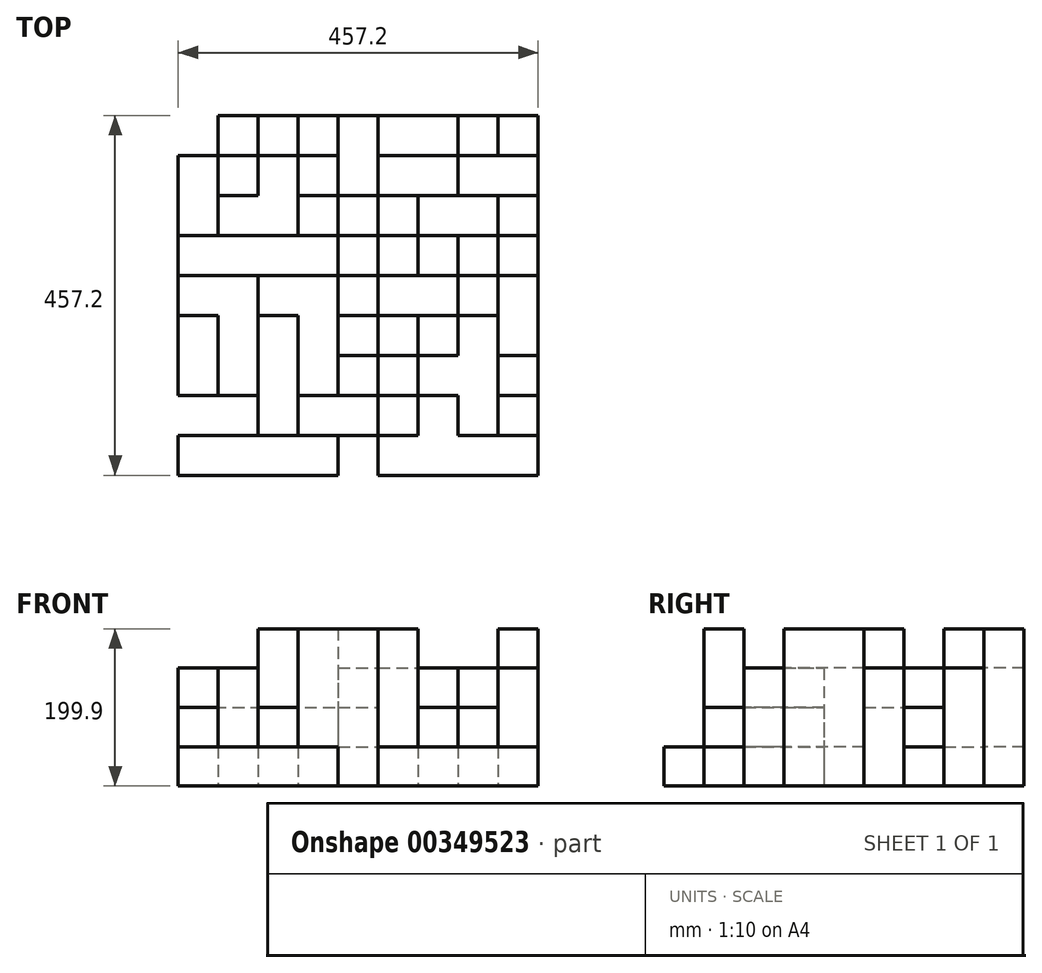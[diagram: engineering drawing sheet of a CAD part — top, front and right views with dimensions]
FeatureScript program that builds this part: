
annotation { "Feature Type Name" : "Feature", "Feature Type Description" : "" }
export const myFeature = defineFeature(function(context is Context, id is Id, definition is map)
    precondition{}
    {
        {
            var Q0;
            Q0=qCreatedBy(makeId("Top.planeOp"),FACE);
            var sketch = newSketch(context, id + "F0", { "sketchPlane" : qUnion([Q0])});
            skLineSegment(sketch, "E0.bottom", {"start": v(-228.6, 228.6) * mm, "end": v(228.6, 228.6) * mm});
            skLineSegment(sketch, "E0.top", {"start": v(-228.6, -228.6) * mm, "end": v(228.6, -228.6) * mm});
            skLineSegment(sketch, "E0.left", {"start": v(-228.6, 228.6) * mm, "end": v(-228.6, -228.6) * mm});
            skLineSegment(sketch, "E0.right", {"start": v(228.6, 228.6) * mm, "end": v(228.6, -228.6) * mm});
            skPoint(sketch, "E0.middle", {"position": v(0, 0) * mm});
            skLineSegment(sketch, "E1.bottom", {"start": v(-228.6, 228.6) * mm, "end": v(-177.8, 228.6) * mm});
            skLineSegment(sketch, "E1.top", {"start": v(-228.6, 177.8) * mm, "end": v(-177.8, 177.8) * mm});
            skLineSegment(sketch, "E1.left", {"start": v(-228.6, 228.6) * mm, "end": v(-228.6, 177.8) * mm});
            skLineSegment(sketch, "E1.right", {"start": v(-177.8, 228.6) * mm, "end": v(-177.8, 177.8) * mm});
            skLineSegment(sketch, "E2.MirrorCS", {"start": v(685.8, 177.8) * mm, "end": v(635, 177.8) * mm});
            skLineSegment(sketch, "E3.MirrorCS", {"start": v(635, 228.6) * mm, "end": v(635, 177.8) * mm});
            skLineSegment(sketch, "E4.bottom", {"start": v(-177.8, 228.6) * mm, "end": v(-127, 228.6) * mm});
            skLineSegment(sketch, "E4.top", {"start": v(-177.8, 177.8) * mm, "end": v(-127, 177.8) * mm});
            skLineSegment(sketch, "E4.right", {"start": v(-127, 228.6) * mm, "end": v(-127, 177.8) * mm});
            skLineSegment(sketch, "E5.bottom", {"start": v(-127, 177.8) * mm, "end": v(-76.2, 177.8) * mm});
            skLineSegment(sketch, "E5.top", {"start": v(-127, 228.6) * mm, "end": v(-76.2, 228.6) * mm});
            skLineSegment(sketch, "E5.left", {"start": v(-127, 177.8) * mm, "end": v(-127, 228.6) * mm});
            skLineSegment(sketch, "E6.bottom", {"start": v(-76.2, 228.6) * mm, "end": v(-25.4, 228.6) * mm});
            skLineSegment(sketch, "E6.right", {"start": v(-25.4, 228.6) * mm, "end": v(-25.4, 177.8) * mm});
            skLineSegment(sketch, "E7.bottom", {"start": v(-25.4, 228.6) * mm, "end": v(25.4, 228.6) * mm});
            skLineSegment(sketch, "E7.top", {"start": v(-25.4, 177.8) * mm, "end": v(25.4, 177.8) * mm});
            skLineSegment(sketch, "E7.right", {"start": v(25.4, 228.6) * mm, "end": v(25.4, 177.8) * mm});
            skLineSegment(sketch, "E8.bottom", {"start": v(25.42, 228.6) * mm, "end": v(76.22, 228.6) * mm});
            skLineSegment(sketch, "E8.top", {"start": v(25.42, 177.8) * mm, "end": v(76.22, 177.8) * mm});
            skLineSegment(sketch, "E8.left", {"start": v(25.42, 228.6) * mm, "end": v(25.42, 177.8) * mm});
            skLineSegment(sketch, "E8.right", {"start": v(76.22, 228.6) * mm, "end": v(76.22, 177.8) * mm});
            skLineSegment(sketch, "E9.bottom", {"start": v(76.22, 228.6) * mm, "end": v(127.02, 228.6) * mm});
            skLineSegment(sketch, "E9.top", {"start": v(76.22, 177.8) * mm, "end": v(127.02, 177.8) * mm});
            skLineSegment(sketch, "E9.right", {"start": v(127.02, 228.6) * mm, "end": v(127.02, 177.8) * mm});
            skLineSegment(sketch, "E10.bottom", {"start": v(127.02, 228.6) * mm, "end": v(177.82, 228.6) * mm});
            skLineSegment(sketch, "E10.top", {"start": v(127.02, 177.8) * mm, "end": v(177.82, 177.8) * mm});
            skLineSegment(sketch, "E10.right", {"start": v(177.82, 228.6) * mm, "end": v(177.82, 177.8) * mm});
            skLineSegment(sketch, "E11.bottom", {"start": v(177.82, 228.6) * mm, "end": v(228.62, 228.6) * mm});
            skLineSegment(sketch, "E11.top", {"start": v(177.82, 177.8) * mm, "end": v(228.62, 177.8) * mm});
            skLineSegment(sketch, "E11.right", {"start": v(228.62, 228.6) * mm, "end": v(228.62, 177.8) * mm});
            skLineSegment(sketch, "E12", {"start": v(-76.2, 228.6) * mm, "end": v(-76.2, 177.8) * mm});
            skLineSegment(sketch, "E13.bottom", {"start": v(-76.2, 177.8) * mm, "end": v(-25.4, 177.8) * mm});
            skLineSegment(sketch, "E13.top", {"start": v(-76.2, 177.8) * mm, "end": v(-25.4, 177.8) * mm});
            skLineSegment(sketch, "E13.left", {"start": v(-76.2, 177.8) * mm, "end": v(-76.2, 177.8) * mm});
            skLineSegment(sketch, "E13.right", {"start": v(-25.4, 177.8) * mm, "end": v(-25.4, 177.8) * mm});
            skLineSegment(sketch, "E14.MirrorCS", {"start": v(-228.6, 127) * mm, "end": v(-228.6, 177.8) * mm});
            skLineSegment(sketch, "E15.MirrorCS", {"start": v(-127, 127) * mm, "end": v(-127, 177.8) * mm});
            skLineSegment(sketch, "E16.MirrorCS", {"start": v(-76.2, 127) * mm, "end": v(-76.2, 177.8) * mm});
            skLineSegment(sketch, "E17.MirrorCS", {"start": v(-25.4, 127) * mm, "end": v(-25.4, 177.8) * mm});
            skLineSegment(sketch, "E18.MirrorCS", {"start": v(25.42, 127) * mm, "end": v(25.42, 177.8) * mm});
            skLineSegment(sketch, "E19.MirrorCS", {"start": v(-228.6, 127) * mm, "end": v(-177.8, 127) * mm});
            skLineSegment(sketch, "E20.MirrorCS", {"start": v(-127, 177.8) * mm, "end": v(-127, 127) * mm});
            skLineSegment(sketch, "E21.MirrorCS", {"start": v(127.02, 127) * mm, "end": v(127.02, 177.8) * mm});
            skLineSegment(sketch, "E22.MirrorCS", {"start": v(25.4, 127) * mm, "end": v(25.4, 177.8) * mm});
            skLineSegment(sketch, "E23.MirrorCS", {"start": v(-177.8, 127) * mm, "end": v(-177.8, 177.8) * mm});
            skLineSegment(sketch, "E24.MirrorCS", {"start": v(-177.8, 127) * mm, "end": v(-127, 127) * mm});
            skLineSegment(sketch, "E25.MirrorCS", {"start": v(76.22, 127) * mm, "end": v(76.22, 177.8) * mm});
            skLineSegment(sketch, "E26.MirrorCS", {"start": v(-25.4, 127) * mm, "end": v(25.4, 127) * mm});
            skLineSegment(sketch, "E27.MirrorCS", {"start": v(25.42, 127) * mm, "end": v(76.22, 127) * mm});
            skLineSegment(sketch, "E28.MirrorCS", {"start": v(76.22, 127) * mm, "end": v(127.02, 127) * mm});
            skLineSegment(sketch, "E29.MirrorCS", {"start": v(127.02, 127) * mm, "end": v(177.82, 127) * mm});
            skLineSegment(sketch, "E30.MirrorCS", {"start": v(-127, 127) * mm, "end": v(-76.2, 127) * mm});
            skLineSegment(sketch, "E31.MirrorCS", {"start": v(-228.6, 127) * mm, "end": v(228.6, 127) * mm});
            skLineSegment(sketch, "E32.MirrorCS", {"start": v(-76.2, 127) * mm, "end": v(-25.4, 127) * mm});
            skLineSegment(sketch, "E33.MirrorCS", {"start": v(177.82, 127) * mm, "end": v(177.82, 177.8) * mm});
            skLineSegment(sketch, "E34.MirrorCS", {"start": v(-76.2, 127) * mm, "end": v(-76.2, 76.2) * mm});
            skLineSegment(sketch, "E35.MirrorCS", {"start": v(-76.2, 25.4) * mm, "end": v(-76.2, 76.2) * mm});
            skLineSegment(sketch, "E36.MirrorCS", {"start": v(-177.8, 76.2) * mm, "end": v(-127, 76.2) * mm});
            skLineSegment(sketch, "E37.MirrorCS", {"start": v(-76.2, 76.2) * mm, "end": v(-25.4, 76.2) * mm});
            skLineSegment(sketch, "E38.MirrorCS", {"start": v(-25.4, 127) * mm, "end": v(-25.4, 76.2) * mm});
            skLineSegment(sketch, "E39.MirrorCS", {"start": v(-127, 25.4) * mm, "end": v(-127, 76.2) * mm});
            skLineSegment(sketch, "E40.MirrorCS", {"start": v(25.4, 25.4) * mm, "end": v(25.4, 76.2) * mm});
            skLineSegment(sketch, "E41.MirrorCS", {"start": v(-127, 127) * mm, "end": v(-127, 76.2) * mm});
            skLineSegment(sketch, "E42.MirrorCS", {"start": v(-25.4, 25.4) * mm, "end": v(-25.4, 76.2) * mm});
            skLineSegment(sketch, "E43.MirrorCS", {"start": v(25.4, 127) * mm, "end": v(25.4, 76.2) * mm});
            skLineSegment(sketch, "E44.MirrorCS", {"start": v(76.22, 127) * mm, "end": v(76.22, 76.2) * mm});
            skLineSegment(sketch, "E45.MirrorCS", {"start": v(-127, 76.2) * mm, "end": v(-127, 127) * mm});
            skLineSegment(sketch, "E46.MirrorCS", {"start": v(127.02, 127) * mm, "end": v(127.02, 76.2) * mm});
            skLineSegment(sketch, "E47.MirrorCS", {"start": v(76.22, 25.4) * mm, "end": v(76.22, 76.2) * mm});
            skLineSegment(sketch, "E48.MirrorCS", {"start": v(-25.4, 76.2) * mm, "end": v(25.4, 76.2) * mm});
            skLineSegment(sketch, "E49.MirrorCS", {"start": v(-25.4, 76.2) * mm, "end": v(-25.4, 76.2) * mm});
            skLineSegment(sketch, "E50.MirrorCS", {"start": v(-177.8, 25.4) * mm, "end": v(-177.8, 76.2) * mm});
            skLineSegment(sketch, "E51.MirrorCS", {"start": v(127.02, 76.2) * mm, "end": v(177.82, 76.2) * mm});
            skLineSegment(sketch, "E52.MirrorCS", {"start": v(25.42, 127) * mm, "end": v(25.42, 76.2) * mm});
            skLineSegment(sketch, "E53.MirrorCS", {"start": v(76.22, 76.2) * mm, "end": v(127.02, 76.2) * mm});
            skLineSegment(sketch, "E54.MirrorCS", {"start": v(-127, 76.2) * mm, "end": v(-127, 25.4) * mm});
            skLineSegment(sketch, "E55.MirrorCS", {"start": v(-76.2, 76.2) * mm, "end": v(-76.2, 76.2) * mm});
            skLineSegment(sketch, "E56.MirrorCS", {"start": v(25.42, 76.2) * mm, "end": v(76.22, 76.2) * mm});
            skLineSegment(sketch, "E57.MirrorCS", {"start": v(25.42, 25.4) * mm, "end": v(25.42, 76.2) * mm});
            skLineSegment(sketch, "E58.MirrorCS", {"start": v(127.02, 25.4) * mm, "end": v(127.02, 76.2) * mm});
            skLineSegment(sketch, "E59.MirrorCS", {"start": v(-177.8, 127) * mm, "end": v(-177.8, 76.2) * mm});
            skLineSegment(sketch, "E60.MirrorCS", {"start": v(-127, 76.2) * mm, "end": v(-76.2, 76.2) * mm});
            skLineSegment(sketch, "E61.MirrorCS", {"start": v(177.82, 25.4) * mm, "end": v(177.82, 76.2) * mm});
            skLineSegment(sketch, "E62.MirrorCS", {"start": v(-177.8, 25.4) * mm, "end": v(-127, 25.4) * mm});
            skLineSegment(sketch, "E63.MirrorCS", {"start": v(-25.4, 25.4) * mm, "end": v(25.4, 25.4) * mm});
            skLineSegment(sketch, "E64.MirrorCS", {"start": v(-76.2, 25.4) * mm, "end": v(-25.4, 25.4) * mm});
            skLineSegment(sketch, "E65.MirrorCS", {"start": v(76.22, 25.4) * mm, "end": v(127.02, 25.4) * mm});
            skLineSegment(sketch, "E66.MirrorCS", {"start": v(25.42, 25.4) * mm, "end": v(76.22, 25.4) * mm});
            skLineSegment(sketch, "E67.MirrorCS", {"start": v(127.02, 25.4) * mm, "end": v(177.82, 25.4) * mm});
            skLineSegment(sketch, "E68.MirrorCS", {"start": v(-127, 25.4) * mm, "end": v(-76.2, 25.4) * mm});
            skLineSegment(sketch, "E69.MirrorCS", {"start": v(177.82, 127) * mm, "end": v(177.82, 76.2) * mm});
            skLineSegment(sketch, "E70.MirrorCS", {"start": v(177.82, 76.2) * mm, "end": v(228.62, 76.2) * mm});
            skLineSegment(sketch, "E71.MirrorCS", {"start": v(-228.6, 76.2) * mm, "end": v(-177.8, 76.2) * mm});
            skLineSegment(sketch, "E72.MirrorCS", {"start": v(-228.6, 25.4) * mm, "end": v(-177.8, 25.4) * mm});
            skLineSegment(sketch, "E73.MirrorCS", {"start": v(-228.6, 25.4) * mm, "end": v(228.6, 25.4) * mm});
            skLineSegment(sketch, "E74.MirrorCS", {"start": v(-76.2, -76.2) * mm, "end": v(-76.2, -25.4) * mm});
            skLineSegment(sketch, "E75.MirrorCS", {"start": v(-76.2, -76.2) * mm, "end": v(-76.2, -127) * mm});
            skLineSegment(sketch, "E76.MirrorCS", {"start": v(-76.2, -177.8) * mm, "end": v(-76.2, -127) * mm});
            skLineSegment(sketch, "E77.MirrorCS", {"start": v(-76.2, -25.4) * mm, "end": v(-25.4, -25.4) * mm});
            skLineSegment(sketch, "E78.MirrorCS", {"start": v(-177.8, -25.4) * mm, "end": v(-127, -25.4) * mm});
            skLineSegment(sketch, "E79.MirrorCS", {"start": v(-76.2, -177.8) * mm, "end": v(-25.4, -177.8) * mm});
            skLineSegment(sketch, "E80.MirrorCS", {"start": v(-127, -177.8) * mm, "end": v(-76.2, -177.8) * mm});
            skLineSegment(sketch, "E81.MirrorCS", {"start": v(-76.2, -127) * mm, "end": v(-25.4, -127) * mm});
            skLineSegment(sketch, "E82.MirrorCS", {"start": v(127.02, -177.8) * mm, "end": v(177.82, -177.8) * mm});
            skLineSegment(sketch, "E83.MirrorCS", {"start": v(177.82, -177.8) * mm, "end": v(228.62, -177.8) * mm});
            skLineSegment(sketch, "E84.MirrorCS", {"start": v(-25.4, -177.8) * mm, "end": v(25.4, -177.8) * mm});
            skLineSegment(sketch, "E85.MirrorCS", {"start": v(-177.8, -127) * mm, "end": v(-127, -127) * mm});
            skLineSegment(sketch, "E86.MirrorCS", {"start": v(76.22, -76.2) * mm, "end": v(127.02, -76.2) * mm});
            skLineSegment(sketch, "E87.MirrorCS", {"start": v(25.42, -76.2) * mm, "end": v(76.22, -76.2) * mm});
            skLineSegment(sketch, "E88.MirrorCS", {"start": v(-127, -177.8) * mm, "end": v(-127, -127) * mm});
            skLineSegment(sketch, "E89.MirrorCS", {"start": v(-25.4, -76.2) * mm, "end": v(-25.4, -25.4) * mm});
            skLineSegment(sketch, "E90.MirrorCS", {"start": v(25.42, -177.8) * mm, "end": v(25.42, -127) * mm});
            skLineSegment(sketch, "E91.MirrorCS", {"start": v(25.42, -76.2) * mm, "end": v(25.42, -127) * mm});
            skLineSegment(sketch, "E92.MirrorCS", {"start": v(-127, -25.4) * mm, "end": v(-127, -76.2) * mm});
            skLineSegment(sketch, "E93.MirrorCS", {"start": v(-127, -76.2) * mm, "end": v(-127, -127) * mm});
            skLineSegment(sketch, "E94.MirrorCS", {"start": v(-25.4, -76.2) * mm, "end": v(-25.4, -127) * mm});
            skLineSegment(sketch, "E95.MirrorCS", {"start": v(-25.4, -177.8) * mm, "end": v(-25.4, -127) * mm});
            skLineSegment(sketch, "E96.MirrorCS", {"start": v(-228.6, -177.8) * mm, "end": v(228.6, -177.8) * mm});
            skLineSegment(sketch, "E97.MirrorCS", {"start": v(25.42, -76.2) * mm, "end": v(25.42, -25.4) * mm});
            skLineSegment(sketch, "E98.MirrorCS", {"start": v(127.02, -76.2) * mm, "end": v(177.82, -76.2) * mm});
            skLineSegment(sketch, "E99.MirrorCS", {"start": v(-177.8, -76.2) * mm, "end": v(-127, -76.2) * mm});
            skLineSegment(sketch, "E100.MirrorCS", {"start": v(25.42, -177.8) * mm, "end": v(76.22, -177.8) * mm});
            skLineSegment(sketch, "E101.MirrorCS", {"start": v(-127, -76.2) * mm, "end": v(-76.2, -76.2) * mm});
            skLineSegment(sketch, "E102.MirrorCS", {"start": v(-127, -76.2) * mm, "end": v(-127, -25.4) * mm});
            skLineSegment(sketch, "E103.MirrorCS", {"start": v(-177.8, -76.2) * mm, "end": v(-177.8, -25.4) * mm});
            skLineSegment(sketch, "E104.MirrorCS", {"start": v(-228.6, -76.2) * mm, "end": v(-177.8, -76.2) * mm});
            skLineSegment(sketch, "E105.MirrorCS", {"start": v(-127, -127) * mm, "end": v(-127, -177.8) * mm});
            skLineSegment(sketch, "E106.MirrorCS", {"start": v(76.22, -76.2) * mm, "end": v(76.22, -25.4) * mm});
            skLineSegment(sketch, "E107.MirrorCS", {"start": v(127.02, -127) * mm, "end": v(177.82, -127) * mm});
            skLineSegment(sketch, "E108.MirrorCS", {"start": v(25.4, -76.2) * mm, "end": v(25.4, -127) * mm});
            skLineSegment(sketch, "E109.MirrorCS", {"start": v(-25.4, -127) * mm, "end": v(25.4, -127) * mm});
            skLineSegment(sketch, "E110.MirrorCS", {"start": v(-76.2, -127) * mm, "end": v(-76.2, -127) * mm});
            skLineSegment(sketch, "E111.MirrorCS", {"start": v(76.22, -127) * mm, "end": v(127.02, -127) * mm});
            skLineSegment(sketch, "E112.MirrorCS", {"start": v(-177.8, -76.2) * mm, "end": v(-177.8, -127) * mm});
            skLineSegment(sketch, "E113.MirrorCS", {"start": v(-76.2, -25.4) * mm, "end": v(-76.2, -25.4) * mm});
            skLineSegment(sketch, "E114.MirrorCS", {"start": v(-25.4, -127) * mm, "end": v(-25.4, -127) * mm});
            skLineSegment(sketch, "E115.MirrorCS", {"start": v(127.02, -76.2) * mm, "end": v(127.02, -25.4) * mm});
            skLineSegment(sketch, "E116.MirrorCS", {"start": v(-127, -127) * mm, "end": v(-76.2, -127) * mm});
            skLineSegment(sketch, "E117.MirrorCS", {"start": v(127.02, -177.8) * mm, "end": v(127.02, -127) * mm});
            skLineSegment(sketch, "E118.MirrorCS", {"start": v(76.22, -25.4) * mm, "end": v(127.02, -25.4) * mm});
            skLineSegment(sketch, "E119.MirrorCS", {"start": v(127.02, -25.4) * mm, "end": v(177.82, -25.4) * mm});
            skLineSegment(sketch, "E120.MirrorCS", {"start": v(-127, -25.4) * mm, "end": v(-76.2, -25.4) * mm});
            skLineSegment(sketch, "E121.MirrorCS", {"start": v(-127, -127) * mm, "end": v(-127, -76.2) * mm});
            skLineSegment(sketch, "E122.MirrorCS", {"start": v(177.82, -177.8) * mm, "end": v(177.82, -127) * mm});
            skLineSegment(sketch, "E123.MirrorCS", {"start": v(25.4, -177.8) * mm, "end": v(25.4, -127) * mm});
            skLineSegment(sketch, "E124.MirrorCS", {"start": v(-76.2, -76.2) * mm, "end": v(-25.4, -76.2) * mm});
            skLineSegment(sketch, "E125.MirrorCS", {"start": v(-25.4, -25.4) * mm, "end": v(25.4, -25.4) * mm});
            skLineSegment(sketch, "E126.MirrorCS", {"start": v(127.02, -76.2) * mm, "end": v(127.02, -127) * mm});
            skLineSegment(sketch, "E127.MirrorCS", {"start": v(-25.4, -76.2) * mm, "end": v(25.4, -76.2) * mm});
            skLineSegment(sketch, "E128.MirrorCS", {"start": v(25.42, -127) * mm, "end": v(76.22, -127) * mm});
            skLineSegment(sketch, "E129.MirrorCS", {"start": v(76.22, -76.2) * mm, "end": v(76.22, -127) * mm});
            skLineSegment(sketch, "E130.MirrorCS", {"start": v(25.42, -25.4) * mm, "end": v(76.22, -25.4) * mm});
            skLineSegment(sketch, "E131.MirrorCS", {"start": v(-25.4, -25.4) * mm, "end": v(-25.4, -25.4) * mm});
            skLineSegment(sketch, "E132.MirrorCS", {"start": v(76.22, -177.8) * mm, "end": v(76.22, -127) * mm});
            skLineSegment(sketch, "E133.MirrorCS", {"start": v(-177.8, -177.8) * mm, "end": v(-127, -177.8) * mm});
            skLineSegment(sketch, "E134.MirrorCS", {"start": v(-177.8, -177.8) * mm, "end": v(-177.8, -127) * mm});
            skLineSegment(sketch, "E135.MirrorCS", {"start": v(177.82, -76.2) * mm, "end": v(177.82, -127) * mm});
            skLineSegment(sketch, "E136.MirrorCS", {"start": v(177.82, -76.2) * mm, "end": v(177.82, -25.4) * mm});
            skLineSegment(sketch, "E137.MirrorCS", {"start": v(228.62, -177.8) * mm, "end": v(228.62, -127) * mm});
            skLineSegment(sketch, "E138.MirrorCS", {"start": v(177.82, -127) * mm, "end": v(228.62, -127) * mm});
            skLineSegment(sketch, "E139.MirrorCS", {"start": v(177.82, -25.4) * mm, "end": v(228.62, -25.4) * mm});
            skLineSegment(sketch, "E140.MirrorCS", {"start": v(-228.6, -76.2) * mm, "end": v(-228.6, -127) * mm});
            skLineSegment(sketch, "E141.MirrorCS", {"start": v(-228.6, -25.4) * mm, "end": v(-177.8, -25.4) * mm});
            skLineSegment(sketch, "E142.MirrorCS", {"start": v(-228.6, -177.8) * mm, "end": v(-177.8, -177.8) * mm});
            skLineSegment(sketch, "E143.MirrorCS", {"start": v(-228.6, -127) * mm, "end": v(-177.8, -127) * mm});
            skLineSegment(sketch, "E144.MirrorCS", {"start": v(-228.6, -177.8) * mm, "end": v(-228.6, -127) * mm});
            skLineSegment(sketch, "E145.MirrorCS", {"start": v(-228.6, -76.2) * mm, "end": v(228.6, -76.2) * mm});
            skLineSegment(sketch, "E146.MirrorCS", {"start": v(25.4, -76.2) * mm, "end": v(25.4, -25.4) * mm});
            skLineSegment(sketch, "E147.MirrorCS", {"start": v(76.22, -177.8) * mm, "end": v(127.02, -177.8) * mm});
            skLineSegment(sketch, "E148.MirrorCS", {"start": v(-76.2, 25.4) * mm, "end": v(-76.2, -25.4) * mm});
            skLineSegment(sketch, "E149.MirrorCS", {"start": v(-25.4, 25.4) * mm, "end": v(-25.4, -25.4) * mm});
            skLineSegment(sketch, "E150.MirrorCS", {"start": v(25.4, 25.4) * mm, "end": v(25.4, -25.4) * mm});
            skLineSegment(sketch, "E151.MirrorCS", {"start": v(-127, 25.4) * mm, "end": v(-127, -25.4) * mm});
            skLineSegment(sketch, "E152.MirrorCS", {"start": v(-177.8, 25.4) * mm, "end": v(-177.8, -25.4) * mm});
            skLineSegment(sketch, "E153.MirrorCS", {"start": v(177.82, 25.4) * mm, "end": v(177.82, -25.4) * mm});
            skLineSegment(sketch, "E154.MirrorCS", {"start": v(-127, -25.4) * mm, "end": v(-127, 25.4) * mm});
            skLineSegment(sketch, "E155.MirrorCS", {"start": v(76.22, 25.4) * mm, "end": v(76.22, -25.4) * mm});
            skLineSegment(sketch, "E156.MirrorCS", {"start": v(127.02, 25.4) * mm, "end": v(127.02, -25.4) * mm});
            skLineSegment(sketch, "E157.MirrorCS", {"start": v(25.42, 25.4) * mm, "end": v(25.42, -25.4) * mm});
            skLineSegment(sketch, "E158.MirrorCS", {"start": v(-76.2, -228.6) * mm, "end": v(-25.4, -228.6) * mm});
            skLineSegment(sketch, "E159.MirrorCS", {"start": v(-177.8, -228.6) * mm, "end": v(-127, -228.6) * mm});
            skLineSegment(sketch, "E160.MirrorCS", {"start": v(-25.4, -228.6) * mm, "end": v(-25.4, -228.6) * mm});
            skLineSegment(sketch, "E161.MirrorCS", {"start": v(127.02, -228.6) * mm, "end": v(177.82, -228.6) * mm});
            skLineSegment(sketch, "E162.MirrorCS", {"start": v(-25.4, -228.6) * mm, "end": v(25.4, -228.6) * mm});
            skLineSegment(sketch, "E163.MirrorCS", {"start": v(-127, -228.6) * mm, "end": v(-76.2, -228.6) * mm});
            skLineSegment(sketch, "E164.MirrorCS", {"start": v(76.22, -228.6) * mm, "end": v(127.02, -228.6) * mm});
            skLineSegment(sketch, "E165.MirrorCS", {"start": v(-76.2, -228.6) * mm, "end": v(-76.2, -228.6) * mm});
            skLineSegment(sketch, "E166.MirrorCS", {"start": v(25.42, -228.6) * mm, "end": v(76.22, -228.6) * mm});
            skLineSegment(sketch, "E167.MirrorCS", {"start": v(177.82, -228.6) * mm, "end": v(228.62, -228.6) * mm});
            skLineSegment(sketch, "E168.MirrorCS", {"start": v(-228.6, -228.6) * mm, "end": v(-177.8, -228.6) * mm});
            skLineSegment(sketch, "E169.MirrorCS", {"start": v(177.82, -177.8) * mm, "end": v(177.82, -228.6) * mm});
            skLineSegment(sketch, "E170.MirrorCS", {"start": v(127.02, -177.8) * mm, "end": v(127.02, -228.6) * mm});
            skLineSegment(sketch, "E171.MirrorCS", {"start": v(76.22, -177.8) * mm, "end": v(76.22, -228.6) * mm});
            skLineSegment(sketch, "E172.MirrorCS", {"start": v(25.42, -177.8) * mm, "end": v(25.42, -228.6) * mm});
            skLineSegment(sketch, "E173.MirrorCS", {"start": v(-25.4, -177.8) * mm, "end": v(-25.4, -228.6) * mm});
            skLineSegment(sketch, "E174.MirrorCS", {"start": v(-76.2, -177.8) * mm, "end": v(-76.2, -228.6) * mm});
            skLineSegment(sketch, "E175.MirrorCS", {"start": v(-127, -177.8) * mm, "end": v(-127, -228.6) * mm});
            skLineSegment(sketch, "E176.MirrorCS", {"start": v(-177.8, -177.8) * mm, "end": v(-177.8, -228.6) * mm});
            skSolve(sketch);
        }
        {
            var Q0;
            {var subQ0=sQuery(id+"F0.wireOp",EDGE,"E50.MirrorCS");Q0=makeQuery(id+"F0.imprint","IMPRINT",FACE,{"disambiguationData":[TD([[makeQuery(id+"F0.imprint","IMPRINT",EDGE,{"derivedFrom":subQ0}),-1.0]])]});}
            var Q1;
            Q1=sQuery(id+"F0.wireOp",EDGE,"E0.top");
            revolve(context, id + "F1", {"entities" : qUnion([Q0]), "axis" : qUnion([Q1]), "revolveType" : RevolveType.FULL});
        }
        {
            var Q0;
            Q0=makeQuery(id+"F1.opRevolve","SWEPT_BODY",BODY,{"disambiguationData":[OSD([sQuery(id+"F0.wireOp",EDGE,"E50.MirrorCS"),sQuery(id+"F0.wireOp",EDGE,"E36.MirrorCS"),sQuery(id+"F0.wireOp",EDGE,"E39.MirrorCS"),sQuery(id+"F0.wireOp",EDGE,"E73.MirrorCS")])]});
            deleteBodies(context, id + "F2", {"entities" : qUnion([Q0])});
        }
        {
            var Q0;
            Q0=makeQuery(id+"F0.imprint","IMPRINT",FACE,{"disambiguationData":[TD([[makeQuery(id+"F0.imprint","IMPRINT",EDGE,{"derivedFrom":sQuery(id+"F0.wireOp",EDGE,"E13.bottom")}),1.0]])]});
            var Q1;
            {var subQ0=sQuery(id+"F0.wireOp",EDGE,"E9.right");Q1=makeQuery(id+"F0.imprint","IMPRINT",FACE,{"disambiguationData":[TD([[makeQuery(id+"F0.imprint","IMPRINT",EDGE,{"derivedFrom":subQ0}),1.0]])]});}
            var Q2;
            Q2=makeQuery(id+"F0.imprint","IMPRINT",FACE,{"disambiguationData":[TD([[makeQuery(id+"F0.imprint","IMPRINT",EDGE,{"derivedFrom":sQuery(id+"F0.wireOp",EDGE,"E15.MirrorCS")}),-1.0]])]});
            var Q3;
            Q3=makeQuery(id+"F0.imprint","IMPRINT",FACE,{"disambiguationData":[TD([[makeQuery(id+"F0.imprint","IMPRINT",EDGE,{"derivedFrom":sQuery(id+"F0.wireOp",EDGE,"E36.MirrorCS")}),1.0]])]});
            var Q4;
            Q4=makeQuery(id+"F0.imprint","IMPRINT",FACE,{"disambiguationData":[TD([[makeQuery(id+"F0.imprint","IMPRINT",EDGE,{"derivedFrom":sQuery(id+"F0.wireOp",EDGE,"E30.MirrorCS")}),-1.0]])]});
            var Q5;
            Q5=makeQuery(id+"F0.imprint","IMPRINT",FACE,{"disambiguationData":[TD([[makeQuery(id+"F0.imprint","IMPRINT",EDGE,{"derivedFrom":sQuery(id+"F0.wireOp",EDGE,"E18.MirrorCS")}),-1.0]])]});
            var Q6;
            Q6=makeQuery(id+"F0.imprint","IMPRINT",FACE,{"disambiguationData":[TD([[makeQuery(id+"F0.imprint","IMPRINT",EDGE,{"derivedFrom":sQuery(id+"F0.wireOp",EDGE,"E21.MirrorCS")}),1.0]])]});
            var Q7;
            {var subQ5=sQuery(id+"F0.wireOp",EDGE,"E69.MirrorCS");Q7=makeQuery(id+"F0.imprint","IMPRINT",FACE,{"disambiguationData":[TD([[makeQuery(id+"F0.imprint","IMPRINT",EDGE,{"derivedFrom":subQ5}),1.0]])]});}
            var Q8;
            Q8=makeQuery(id+"F0.imprint","IMPRINT",FACE,{"disambiguationData":[TD([[makeQuery(id+"F0.imprint","IMPRINT",EDGE,{"derivedFrom":sQuery(id+"F0.wireOp",EDGE,"E43.MirrorCS")}),-1.0]])]});
            var Q9;
            Q9=makeQuery(id+"F0.imprint","IMPRINT",FACE,{"disambiguationData":[TD([[makeQuery(id+"F0.imprint","IMPRINT",EDGE,{"derivedFrom":sQuery(id+"F0.wireOp",EDGE,"E77.MirrorCS")}),1.0]])]});
            var Q10;
            Q10=makeQuery(id+"F0.imprint","IMPRINT",FACE,{"disambiguationData":[TD([[makeQuery(id+"F0.imprint","IMPRINT",EDGE,{"derivedFrom":sQuery(id+"F0.wireOp",EDGE,"E120.MirrorCS")}),1.0]])]});
            var Q11;
            Q11=makeQuery(id+"F0.imprint","IMPRINT",FACE,{"disambiguationData":[TD([[makeQuery(id+"F0.imprint","IMPRINT",EDGE,{"derivedFrom":sQuery(id+"F0.wireOp",EDGE,"E130.MirrorCS")}),1.0]])]});
            var Q12;
            Q12=makeQuery(id+"F0.imprint","IMPRINT",FACE,{"disambiguationData":[TD([[makeQuery(id+"F0.imprint","IMPRINT",EDGE,{"derivedFrom":sQuery(id+"F0.wireOp",EDGE,"E118.MirrorCS")}),1.0]])]});
            var Q13;
            Q13=makeQuery(id+"F0.imprint","IMPRINT",FACE,{"disambiguationData":[TD([[makeQuery(id+"F0.imprint","IMPRINT",EDGE,{"derivedFrom":sQuery(id+"F0.wireOp",EDGE,"E77.MirrorCS")}),-1.0]])]});
            var Q14;
            Q14=makeQuery(id+"F0.imprint","IMPRINT",FACE,{"disambiguationData":[TD([[makeQuery(id+"F0.imprint","IMPRINT",EDGE,{"derivedFrom":sQuery(id+"F0.wireOp",EDGE,"E94.MirrorCS")}),-1.0]])]});
            var Q15;
            Q15=makeQuery(id+"F0.imprint","IMPRINT",FACE,{"disambiguationData":[TD([[makeQuery(id+"F0.imprint","IMPRINT",EDGE,{"derivedFrom":sQuery(id+"F0.wireOp",EDGE,"E128.MirrorCS")}),1.0]])]});
            var Q16;
            Q16=makeQuery(id+"F0.imprint","IMPRINT",FACE,{"disambiguationData":[TD([[makeQuery(id+"F0.imprint","IMPRINT",EDGE,{"derivedFrom":sQuery(id+"F0.wireOp",EDGE,"E117.MirrorCS")}),1.0]])]});
            var Q17;
            Q17=makeQuery(id+"F0.imprint","IMPRINT",FACE,{"disambiguationData":[TD([[makeQuery(id+"F0.imprint","IMPRINT",EDGE,{"derivedFrom":sQuery(id+"F0.wireOp",EDGE,"E0.top")}),1.0]])]});
            var Q18;
            Q18=makeQuery(id+"F0.imprint","IMPRINT",FACE,{"disambiguationData":[TD([[makeQuery(id+"F0.imprint","IMPRINT",EDGE,{"derivedFrom":sQuery(id+"F0.wireOp",EDGE,"E161.MirrorCS")}),1.0]])]});
            var Q19;
            Q19=makeQuery(id+"F0.imprint","IMPRINT",FACE,{"disambiguationData":[TD([[makeQuery(id+"F0.imprint","IMPRINT",EDGE,{"derivedFrom":sQuery(id+"F0.wireOp",EDGE,"E163.MirrorCS")}),1.0]])]});
            extrude(context, id + "F3", {"entities" : qUnion([Q0, Q1, Q2, Q3, Q4, Q5, Q6, Q7, Q8, Q9, Q10, Q11, Q12, Q13, Q14, Q15, Q16, Q17, Q18, Q19]), "depth" : 50.04 * mm});
        }
        {
            var Q0;
            {var subQ0=sQuery(id+"F0.wireOp",EDGE,"E7.right");Q0=makeQuery(id+"F0.imprint","IMPRINT",FACE,{"disambiguationData":[TD([[makeQuery(id+"F0.imprint","IMPRINT",EDGE,{"derivedFrom":subQ0}),-1.0]])]});}
            var Q1;
            Q1=makeQuery(id+"F0.imprint","IMPRINT",FACE,{"disambiguationData":[TD([[makeQuery(id+"F0.imprint","IMPRINT",EDGE,{"derivedFrom":sQuery(id+"F0.wireOp",EDGE,"E22.MirrorCS")}),1.0]])]});
            var Q2;
            Q2=makeQuery(id+"F0.imprint","IMPRINT",FACE,{"disambiguationData":[TD([[makeQuery(id+"F0.imprint","IMPRINT",EDGE,{"derivedFrom":sQuery(id+"F0.wireOp",EDGE,"E53.MirrorCS")}),1.0]])]});
            var Q3;
            Q3=makeQuery(id+"F0.imprint","IMPRINT",FACE,{"disambiguationData":[TD([[makeQuery(id+"F0.imprint","IMPRINT",EDGE,{"derivedFrom":sQuery(id+"F0.wireOp",EDGE,"E56.MirrorCS")}),1.0]])]});
            var Q4;
            {var subQ0=sQuery(id+"F0.wireOp",EDGE,"E50.MirrorCS");Q4=makeQuery(id+"F0.imprint","IMPRINT",FACE,{"disambiguationData":[TD([[makeQuery(id+"F0.imprint","IMPRINT",EDGE,{"derivedFrom":subQ0}),-1.0]])]});}
            var Q5;
            Q5=makeQuery(id+"F0.imprint","IMPRINT",FACE,{"disambiguationData":[TD([[makeQuery(id+"F0.imprint","IMPRINT",EDGE,{"derivedFrom":sQuery(id+"F0.wireOp",EDGE,"E60.MirrorCS")}),-1.0]])]});
            var Q6;
            {var subQ4=sQuery(id+"F0.wireOp",EDGE,"E50.MirrorCS");Q6=makeQuery(id+"F0.imprint","IMPRINT",FACE,{"disambiguationData":[TD([[makeQuery(id+"F0.imprint","IMPRINT",EDGE,{"derivedFrom":subQ4}),1.0]])]});}
            var Q7;
            {var subQ0=sQuery(id+"F0.wireOp",EDGE,"E42.MirrorCS");Q7=makeQuery(id+"F0.imprint","IMPRINT",FACE,{"disambiguationData":[TD([[makeQuery(id+"F0.imprint","IMPRINT",EDGE,{"derivedFrom":subQ0}),1.0]])]});}
            var Q8;
            Q8=makeQuery(id+"F0.imprint","IMPRINT",FACE,{"disambiguationData":[TD([[makeQuery(id+"F0.imprint","IMPRINT",EDGE,{"derivedFrom":sQuery(id+"F0.wireOp",EDGE,"E51.MirrorCS")}),-1.0]])]});
            var Q9;
            {var subQ4=sQuery(id+"F0.wireOp",EDGE,"E103.MirrorCS");Q9=makeQuery(id+"F0.imprint","IMPRINT",FACE,{"disambiguationData":[TD([[makeQuery(id+"F0.imprint","IMPRINT",EDGE,{"derivedFrom":subQ4}),1.0]])]});}
            var Q10;
            {var subQ0=sQuery(id+"F0.wireOp",EDGE,"E112.MirrorCS");Q10=makeQuery(id+"F0.imprint","IMPRINT",FACE,{"disambiguationData":[TD([[makeQuery(id+"F0.imprint","IMPRINT",EDGE,{"derivedFrom":subQ0}),-1.0]])]});}
            var Q11;
            Q11=makeQuery(id+"F0.imprint","IMPRINT",FACE,{"disambiguationData":[TD([[makeQuery(id+"F0.imprint","IMPRINT",EDGE,{"derivedFrom":sQuery(id+"F0.wireOp",EDGE,"E120.MirrorCS")}),-1.0]])]});
            var Q12;
            Q12=makeQuery(id+"F0.imprint","IMPRINT",FACE,{"disambiguationData":[TD([[makeQuery(id+"F0.imprint","IMPRINT",EDGE,{"derivedFrom":sQuery(id+"F0.wireOp",EDGE,"E116.MirrorCS")}),1.0]])]});
            var Q13;
            {var subQ0=sQuery(id+"F0.wireOp",EDGE,"E115.MirrorCS");Q13=makeQuery(id+"F0.imprint","IMPRINT",FACE,{"disambiguationData":[TD([[makeQuery(id+"F0.imprint","IMPRINT",EDGE,{"derivedFrom":subQ0}),-1.0]])]});}
            var Q14;
            Q14=makeQuery(id+"F0.imprint","IMPRINT",FACE,{"disambiguationData":[TD([[makeQuery(id+"F0.imprint","IMPRINT",EDGE,{"derivedFrom":sQuery(id+"F0.wireOp",EDGE,"E125.MirrorCS")}),-1.0]])]});
            var Q15;
            Q15=makeQuery(id+"F0.imprint","IMPRINT",FACE,{"disambiguationData":[TD([[makeQuery(id+"F0.imprint","IMPRINT",EDGE,{"derivedFrom":sQuery(id+"F0.wireOp",EDGE,"E111.MirrorCS")}),1.0]])]});
            var Q16;
            {var subQ0=sQuery(id+"F0.wireOp",EDGE,"E135.MirrorCS");Q16=makeQuery(id+"F0.imprint","IMPRINT",FACE,{"disambiguationData":[TD([[makeQuery(id+"F0.imprint","IMPRINT",EDGE,{"derivedFrom":subQ0}),-1.0]])]});}
            var Q17;
            Q17=makeQuery(id+"F0.imprint","IMPRINT",FACE,{"disambiguationData":[TD([[makeQuery(id+"F0.imprint","IMPRINT",EDGE,{"derivedFrom":sQuery(id+"F0.wireOp",EDGE,"E142.MirrorCS")}),1.0]])]});
            var Q18;
            Q18=makeQuery(id+"F0.imprint","IMPRINT",FACE,{"disambiguationData":[TD([[makeQuery(id+"F0.imprint","IMPRINT",EDGE,{"derivedFrom":sQuery(id+"F0.wireOp",EDGE,"E116.MirrorCS")}),-1.0]])]});
            var Q19;
            {var subQ0=sQuery(id+"F0.wireOp",EDGE,"E122.MirrorCS");Q19=makeQuery(id+"F0.imprint","IMPRINT",FACE,{"disambiguationData":[TD([[makeQuery(id+"F0.imprint","IMPRINT",EDGE,{"derivedFrom":subQ0}),1.0]])]});}
            extrude(context, id + "F4", {"entities" : qUnion([Q0, Q1, Q2, Q3, Q4, Q5, Q6, Q7, Q8, Q9, Q10, Q11, Q12, Q13, Q14, Q15, Q16, Q17, Q18, Q19]), "depth" : 100.08 * mm});
        }
        {
            var Q0;
            Q0=makeQuery(id+"F4.opExtrude","SWEPT_BODY",BODY,{"disambiguationData":[OSD([sQuery(id+"F0.wireOp",EDGE,"E53.MirrorCS"),sQuery(id+"F0.wireOp",EDGE,"E56.MirrorCS"),sQuery(id+"F0.wireOp",EDGE,"E28.MirrorCS"),sQuery(id+"F0.wireOp",EDGE,"E27.MirrorCS"),sQuery(id+"F0.wireOp",EDGE,"E46.MirrorCS"),sQuery(id+"F0.wireOp",EDGE,"E52.MirrorCS")])]});
            deleteBodies(context, id + "F5", {"entities" : qUnion([Q0])});
        }
        {
            var Q0;
            Q0=makeQuery(id+"F0.imprint","IMPRINT",FACE,{"disambiguationData":[TD([[makeQuery(id+"F0.imprint","IMPRINT",EDGE,{"derivedFrom":sQuery(id+"F0.wireOp",EDGE,"E53.MirrorCS")}),1.0]])]});
            var Q1;
            Q1=makeQuery(id+"F0.imprint","IMPRINT",FACE,{"disambiguationData":[TD([[makeQuery(id+"F0.imprint","IMPRINT",EDGE,{"derivedFrom":sQuery(id+"F0.wireOp",EDGE,"E51.MirrorCS")}),1.0]])]});
            extrude(context, id + "F6", {"entities" : qUnion([Q0, Q1]), "depth" : 100.08 * mm});
        }
        {
            var Q0;
            {var subQ0=sQuery(id+"F0.wireOp",EDGE,"E1.right");Q0=makeQuery(id+"F0.imprint","IMPRINT",FACE,{"disambiguationData":[TD([[makeQuery(id+"F0.imprint","IMPRINT",EDGE,{"derivedFrom":subQ0}),1.0]])]});}
            var Q1;
            Q1=makeQuery(id+"F0.imprint","IMPRINT",FACE,{"disambiguationData":[TD([[makeQuery(id+"F0.imprint","IMPRINT",EDGE,{"derivedFrom":sQuery(id+"F0.wireOp",EDGE,"E1.top")}),-1.0]])]});
            var Q2;
            {var subQ0=sQuery(id+"F0.wireOp",EDGE,"E8.right");Q2=makeQuery(id+"F0.imprint","IMPRINT",FACE,{"disambiguationData":[TD([[makeQuery(id+"F0.imprint","IMPRINT",EDGE,{"derivedFrom":subQ0}),-1.0]])]});}
            var Q3;
            {var subQ0=sQuery(id+"F0.wireOp",EDGE,"E8.right");Q3=makeQuery(id+"F0.imprint","IMPRINT",FACE,{"disambiguationData":[TD([[makeQuery(id+"F0.imprint","IMPRINT",EDGE,{"derivedFrom":subQ0}),1.0]])]});}
            var Q4;
            Q4=makeQuery(id+"F0.imprint","IMPRINT",FACE,{"disambiguationData":[TD([[makeQuery(id+"F0.imprint","IMPRINT",EDGE,{"derivedFrom":sQuery(id+"F0.wireOp",EDGE,"E10.top")}),-1.0]])]});
            var Q5;
            {var subQ5=sQuery(id+"F0.wireOp",EDGE,"E33.MirrorCS");Q5=makeQuery(id+"F0.imprint","IMPRINT",FACE,{"disambiguationData":[TD([[makeQuery(id+"F0.imprint","IMPRINT",EDGE,{"derivedFrom":subQ5}),-1.0]])]});}
            var Q6;
            {var subQ4=sQuery(id+"F0.wireOp",EDGE,"E59.MirrorCS");Q6=makeQuery(id+"F0.imprint","IMPRINT",FACE,{"disambiguationData":[TD([[makeQuery(id+"F0.imprint","IMPRINT",EDGE,{"derivedFrom":subQ4}),-1.0]])]});}
            var Q7;
            Q7=makeQuery(id+"F0.imprint","IMPRINT",FACE,{"disambiguationData":[TD([[makeQuery(id+"F0.imprint","IMPRINT",EDGE,{"derivedFrom":sQuery(id+"F0.wireOp",EDGE,"E32.MirrorCS")}),-1.0]])]});
            var Q8;
            Q8=makeQuery(id+"F0.imprint","IMPRINT",FACE,{"disambiguationData":[TD([[makeQuery(id+"F0.imprint","IMPRINT",EDGE,{"derivedFrom":sQuery(id+"F0.wireOp",EDGE,"E56.MirrorCS")}),1.0]])]});
            var Q9;
            {var subQ0=sQuery(id+"F0.wireOp",EDGE,"E58.MirrorCS");Q9=makeQuery(id+"F0.imprint","IMPRINT",FACE,{"disambiguationData":[TD([[makeQuery(id+"F0.imprint","IMPRINT",EDGE,{"derivedFrom":subQ0}),1.0]])]});}
            var Q10;
            {var subQ5=sQuery(id+"F0.wireOp",EDGE,"E61.MirrorCS");Q10=makeQuery(id+"F0.imprint","IMPRINT",FACE,{"disambiguationData":[TD([[makeQuery(id+"F0.imprint","IMPRINT",EDGE,{"derivedFrom":subQ5}),-1.0]])]});}
            var Q11;
            {var subQ3=sQuery(id+"F0.wireOp",EDGE,"E141.MirrorCS");Q11=makeQuery(id+"F0.imprint","IMPRINT",FACE,{"disambiguationData":[TD([[makeQuery(id+"F0.imprint","IMPRINT",EDGE,{"derivedFrom":subQ3}),1.0]])]});}
            var Q12;
            Q12=makeQuery(id+"F0.imprint","IMPRINT",FACE,{"disambiguationData":[TD([[makeQuery(id+"F0.imprint","IMPRINT",EDGE,{"derivedFrom":sQuery(id+"F0.wireOp",EDGE,"E78.MirrorCS")}),1.0]])]});
            var Q13;
            Q13=makeQuery(id+"F0.imprint","IMPRINT",FACE,{"disambiguationData":[TD([[makeQuery(id+"F0.imprint","IMPRINT",EDGE,{"derivedFrom":sQuery(id+"F0.wireOp",EDGE,"E125.MirrorCS")}),1.0]])]});
            var Q14;
            Q14=makeQuery(id+"F0.imprint","IMPRINT",FACE,{"disambiguationData":[TD([[makeQuery(id+"F0.imprint","IMPRINT",EDGE,{"derivedFrom":sQuery(id+"F0.wireOp",EDGE,"E119.MirrorCS")}),1.0]])]});
            var Q15;
            {var subQ0=sQuery(id+"F0.wireOp",EDGE,"E103.MirrorCS");Q15=makeQuery(id+"F0.imprint","IMPRINT",FACE,{"disambiguationData":[TD([[makeQuery(id+"F0.imprint","IMPRINT",EDGE,{"derivedFrom":subQ0}),-1.0]])]});}
            var Q16;
            {var subQ0=sQuery(id+"F0.wireOp",EDGE,"E112.MirrorCS");Q16=makeQuery(id+"F0.imprint","IMPRINT",FACE,{"disambiguationData":[TD([[makeQuery(id+"F0.imprint","IMPRINT",EDGE,{"derivedFrom":subQ0}),1.0]])]});}
            var Q17;
            {var subQ0=sQuery(id+"F0.wireOp",EDGE,"E115.MirrorCS");Q17=makeQuery(id+"F0.imprint","IMPRINT",FACE,{"disambiguationData":[TD([[makeQuery(id+"F0.imprint","IMPRINT",EDGE,{"derivedFrom":subQ0}),1.0]])]});}
            var Q18;
            Q18=makeQuery(id+"F0.imprint","IMPRINT",FACE,{"disambiguationData":[TD([[makeQuery(id+"F0.imprint","IMPRINT",EDGE,{"derivedFrom":sQuery(id+"F0.wireOp",EDGE,"E108.MirrorCS")}),-1.0]])]});
            var Q19;
            {var subQ2=sQuery(id+"F0.wireOp",EDGE,"E142.MirrorCS");Q19=makeQuery(id+"F0.imprint","IMPRINT",FACE,{"disambiguationData":[TD([[makeQuery(id+"F0.imprint","IMPRINT",EDGE,{"derivedFrom":subQ2}),-1.0]])]});}
            var Q20;
            Q20=makeQuery(id+"F0.imprint","IMPRINT",FACE,{"disambiguationData":[TD([[makeQuery(id+"F0.imprint","IMPRINT",EDGE,{"derivedFrom":sQuery(id+"F0.wireOp",EDGE,"E166.MirrorCS")}),1.0]])]});
            var Q21;
            Q21=makeQuery(id+"F0.imprint","IMPRINT",FACE,{"disambiguationData":[TD([[makeQuery(id+"F0.imprint","IMPRINT",EDGE,{"derivedFrom":sQuery(id+"F0.wireOp",EDGE,"E147.MirrorCS")}),-1.0]])]});
            extrude(context, id + "F7", {"entities" : qUnion([Q0, Q1, Q2, Q3, Q4, Q5, Q6, Q7, Q8, Q9, Q10, Q11, Q12, Q13, Q14, Q15, Q16, Q17, Q18, Q19, Q20, Q21]), "depth" : 149.86 * mm});
        }
        {
            var Q0;
            Q0=makeQuery(id+"F0.imprint","IMPRINT",FACE,{"disambiguationData":[TD([[makeQuery(id+"F0.imprint","IMPRINT",EDGE,{"derivedFrom":sQuery(id+"F0.wireOp",EDGE,"E5.bottom")}),1.0]])]});
            var Q1;
            {var subQ5=sQuery(id+"F0.wireOp",EDGE,"E10.right");Q1=makeQuery(id+"F0.imprint","IMPRINT",FACE,{"disambiguationData":[TD([[makeQuery(id+"F0.imprint","IMPRINT",EDGE,{"derivedFrom":subQ5}),1.0]])]});}
            var Q2;
            Q2=makeQuery(id+"F0.imprint","IMPRINT",FACE,{"disambiguationData":[TD([[makeQuery(id+"F0.imprint","IMPRINT",EDGE,{"derivedFrom":sQuery(id+"F0.wireOp",EDGE,"E13.bottom")}),-1.0]])]});
            var Q3;
            {var subQ0=sQuery(id+"F0.wireOp",EDGE,"E57.MirrorCS");Q3=makeQuery(id+"F0.imprint","IMPRINT",FACE,{"disambiguationData":[TD([[makeQuery(id+"F0.imprint","IMPRINT",EDGE,{"derivedFrom":subQ0}),-1.0]])]});}
            var Q4;
            {var subQ5=sQuery(id+"F0.wireOp",EDGE,"E153.MirrorCS");Q4=makeQuery(id+"F0.imprint","IMPRINT",FACE,{"disambiguationData":[TD([[makeQuery(id+"F0.imprint","IMPRINT",EDGE,{"derivedFrom":subQ5}),1.0]])]});}
            var Q5;
            {var subQ5=sQuery(id+"F0.wireOp",EDGE,"E136.MirrorCS");Q5=makeQuery(id+"F0.imprint","IMPRINT",FACE,{"disambiguationData":[TD([[makeQuery(id+"F0.imprint","IMPRINT",EDGE,{"derivedFrom":subQ5}),-1.0]])]});}
            var Q6;
            {var subQ0=sQuery(id+"F0.wireOp",EDGE,"E95.MirrorCS");Q6=makeQuery(id+"F0.imprint","IMPRINT",FACE,{"disambiguationData":[TD([[makeQuery(id+"F0.imprint","IMPRINT",EDGE,{"derivedFrom":subQ0}),1.0]])]});}
            var Q7;
            {var subQ0=sQuery(id+"F0.wireOp",EDGE,"E123.MirrorCS");Q7=makeQuery(id+"F0.imprint","IMPRINT",FACE,{"disambiguationData":[TD([[makeQuery(id+"F0.imprint","IMPRINT",EDGE,{"derivedFrom":subQ0}),1.0]])]});}
            var Q8;
            Q8=makeQuery(id+"F0.imprint","IMPRINT",FACE,{"disambiguationData":[TD([[makeQuery(id+"F0.imprint","IMPRINT",EDGE,{"derivedFrom":sQuery(id+"F0.wireOp",EDGE,"E159.MirrorCS")}),1.0]])]});
            extrude(context, id + "F8", {"entities" : qUnion([Q0, Q1, Q2, Q3, Q4, Q5, Q6, Q7, Q8]), "depth" : 199.9 * mm});
        }
        {
            var Q0;
            {var subQ5=sQuery(id+"F0.wireOp",EDGE,"E135.MirrorCS");Q0=makeQuery(id+"F0.imprint","IMPRINT",FACE,{"disambiguationData":[TD([[makeQuery(id+"F0.imprint","IMPRINT",EDGE,{"derivedFrom":subQ5}),1.0]])]});}
            extrude(context, id + "F9", {"entities" : qUnion([Q0]), "depth" : 149.86 * mm});
        }
        {
            var Q0;
            {var subQ5=sQuery(id+"F0.wireOp",EDGE,"E122.MirrorCS");Q0=makeQuery(id+"F0.imprint","IMPRINT",FACE,{"disambiguationData":[TD([[makeQuery(id+"F0.imprint","IMPRINT",EDGE,{"derivedFrom":subQ5}),-1.0]])]});}
            extrude(context, id + "F10", {"entities" : qUnion([Q0]), "depth" : 50.04 * mm});
        }
    });
